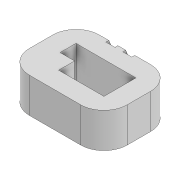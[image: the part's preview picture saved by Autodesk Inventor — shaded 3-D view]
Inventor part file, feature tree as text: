
AUTODESK INVENTOR PART (.ipt)
format: ipt  version: 2021 (Build 250183000, 183)  size: 151,552 bytes
history: native  units: mm
features: extrude x2, sketch x2, fillet x1, chamfer x1
ambient origin geometry x8: Origin, YZ Plane, XZ Plane, XY Plane, X Axis, Y Axis, Z Axis, Center Point
bodies: Volumenkörper1 (feature_tree)
feature tree (6):
  extrude  "Extrusion1"  Depth=12.0mm
  fillet  "Rundung1"  Radius=5.5mm
  extrude  "Extrusion3"  Depth=2.75mm
  chamfer  "Fase2"  Distance=7.8mm
  sketch  "Skizze1"  dims[d0=16.8mm d1=12.0mm d2=5.5mm]
  sketch  "Skizze3"  dims[d3=10.3mm d4=2.75mm d5=7.8mm d6=2.75mm d7=3.25mm d8=3.25mm d9=6.0mm d10=0.0mm d18=4.0mm d21=3.9mm d22=21.554816mm d23=3.9mm d24=21.554816mm d25=7.8mm d26=9.86111mm d27=1.55mm d28=1.55mm d29=1.55mm d30=180.0deg d31=21.554816mm d32=1.55mm d33=3.9mm d34=21.554816mm d35=1.55mm d36=0.0mm d37=1.35mm d38=1.35mm d39=7.35mm d42=3.7mm d43=0.0mm d50=4.725mm d51=4.725mm d52=-0.252155mm d53=0.252155mm d54=0.5mm d55=0.0mm d56=0.5mm d57=2.0mm d58=45.0deg]
